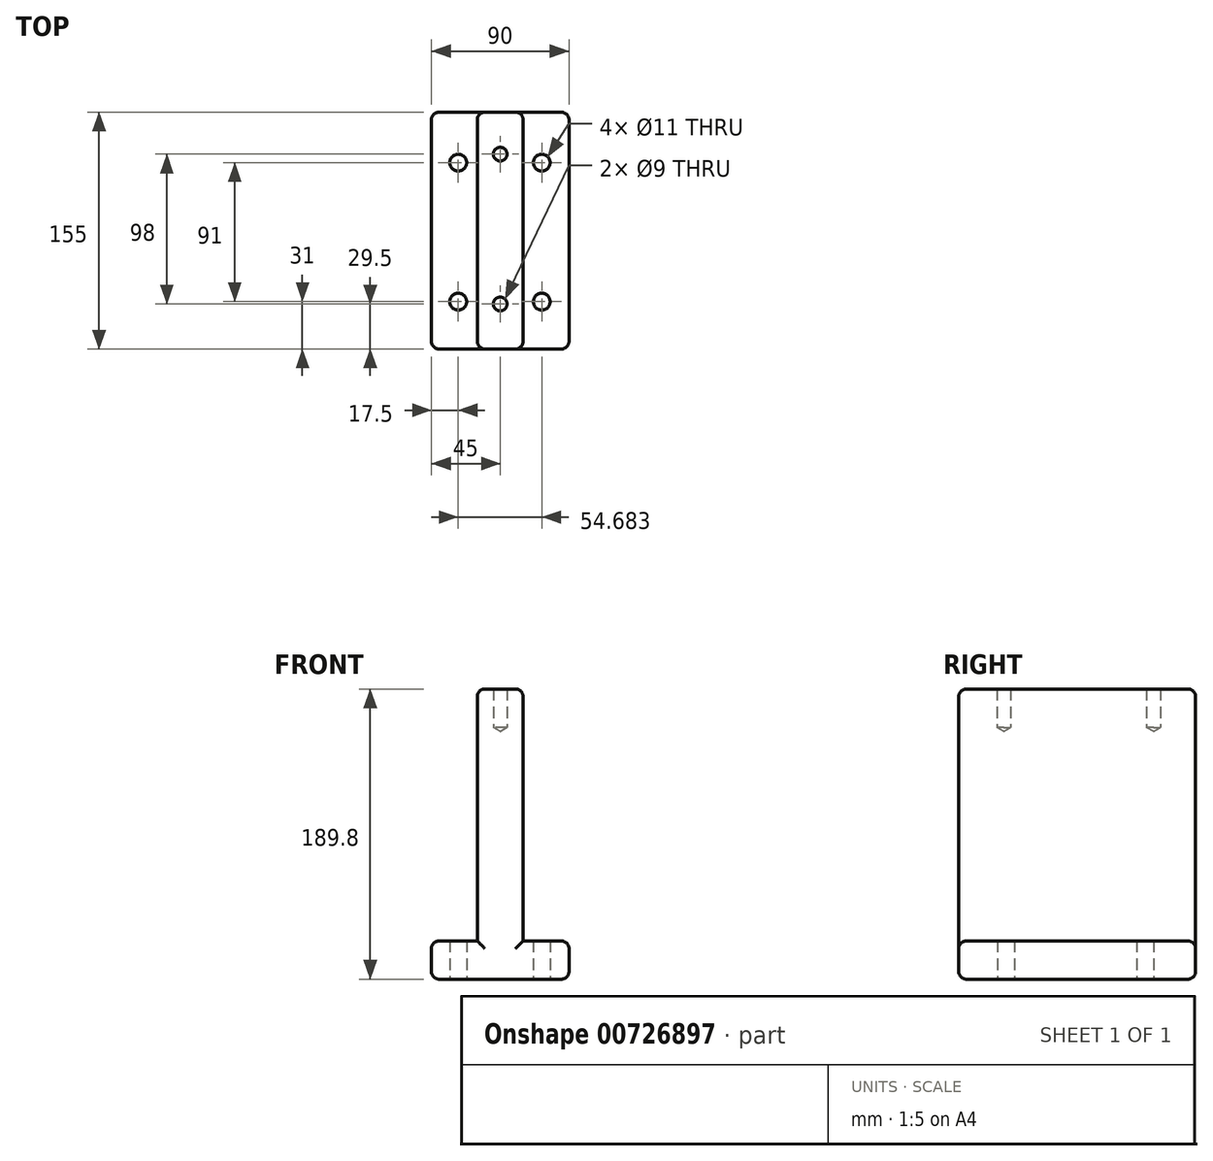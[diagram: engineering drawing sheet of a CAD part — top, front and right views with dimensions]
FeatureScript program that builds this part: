
annotation { "Feature Type Name" : "Feature", "Feature Type Description" : "" }
export const myFeature = defineFeature(function(context is Context, id is Id, definition is map)
    precondition{}
    {
        {
            var Q0;
            Q0=qCreatedBy(makeId("Front.planeOp"),FACE);
            var sketch = newSketch(context, id + "F0", { "sketchPlane" : qUnion([Q0])});
            skLineSegment(sketch, "E0", {"start": v(0, 0) * mm, "end": v(0, 189.8) * mm});
            skLineSegment(sketch, "E1", {"start": v(30, 0) * mm, "end": v(0, 0) * mm});
            skLineSegment(sketch, "E2", {"start": v(30, 0) * mm, "end": v(30, 189.8) * mm});
            skLineSegment(sketch, "E3", {"start": v(30, 189.8) * mm, "end": v(0, 189.8) * mm});
            skLineSegment(sketch, "E4", {"start": v(30, 0) * mm, "end": v(60, 0) * mm});
            skLineSegment(sketch, "E5", {"start": v(60, 0) * mm, "end": v(60, 25) * mm});
            skLineSegment(sketch, "E6", {"start": v(60, 25) * mm, "end": v(30, 25) * mm});
            skLineSegment(sketch, "E7", {"start": v(0, 0) * mm, "end": v(-30, 0) * mm});
            skLineSegment(sketch, "E8", {"start": v(-30, 0) * mm, "end": v(-30, 25) * mm});
            skLineSegment(sketch, "E9", {"start": v(-30, 25) * mm, "end": v(0, 25) * mm});
            skSolve(sketch);
        }
        {
            var Q0;
            Q0 = qSketchRegion(id + "F0", true);
            extrude(context, id + "F1", {"entities" : qUnion([Q0]), "depth" : 155 * mm, "offsetDistance" : 25 * mm});
        }
        {
            var Q0;
            Q0=makeQuery(id+"F1.opExtrude","CAP_EDGE",EDGE,{"disambiguationData":[OSD([sQuery(id+"F0.wireOp",EDGE,"E3")])],"isStart":false});
            var Q1;
            Q1=makeQuery(id+"F1.opExtrude","CAP_EDGE",EDGE,{"disambiguationData":[OSD([sQuery(id+"F0.wireOp",EDGE,"E0")])],"isStart":false});
            var Q2;
            Q2=makeQuery(id+"F1.opExtrude","CAP_EDGE",EDGE,{"disambiguationData":[OSD([sQuery(id+"F0.wireOp",EDGE,"E2")])],"isStart":false});
            var Q3;
            Q3=makeQuery(id+"F1.opExtrude","CAP_EDGE",EDGE,{"disambiguationData":[OSD([sQuery(id+"F0.wireOp",EDGE,"E6")])],"isStart":false});
            var Q4;
            Q4=makeQuery(id+"F1.opExtrude","CAP_EDGE",EDGE,{"disambiguationData":[OSD([sQuery(id+"F0.wireOp",EDGE,"E9")])],"isStart":false});
            var Q5;
            Q5=makeQuery(id+"F1.opExtrude","CAP_EDGE",EDGE,{"disambiguationData":[OSD([sQuery(id+"F0.wireOp",EDGE,"E8")])],"isStart":false});
            var Q6;
            Q6=makeQuery(id+"F1.opExtrude","CAP_EDGE",EDGE,{"disambiguationData":[OSD([sQuery(id+"F0.wireOp",EDGE,"E1"),sQuery(id+"F0.wireOp",EDGE,"E4"),sQuery(id+"F0.wireOp",EDGE,"E7")])],"isStart":false});
            var Q7;
            Q7=makeQuery(id+"F1.opExtrude","CAP_EDGE",EDGE,{"disambiguationData":[OSD([sQuery(id+"F0.wireOp",EDGE,"E5")])],"isStart":false});
            var Q8;
            Q8=makeQuery(id+"F1.opExtrude","SWEPT_EDGE",EDGE,{"disambiguationData":[OSD([sQuery(id+"F0.wireOp",EDGE,"E5"),sQuery(id+"F0.wireOp",EDGE,"E6")])]});
            var Q9;
            Q9=makeQuery(id+"F1.opExtrude","SWEPT_EDGE",EDGE,{"disambiguationData":[OSD([sQuery(id+"F0.wireOp",EDGE,"E4"),sQuery(id+"F0.wireOp",EDGE,"E5")])]});
            var Q10;
            Q10=makeQuery(id+"F1.opExtrude","SWEPT_EDGE",EDGE,{"disambiguationData":[OSD([sQuery(id+"F0.wireOp",EDGE,"E8"),sQuery(id+"F0.wireOp",EDGE,"E9")])]});
            var Q11;
            Q11=makeQuery(id+"F1.opExtrude","SWEPT_EDGE",EDGE,{"disambiguationData":[OSD([sQuery(id+"F0.wireOp",EDGE,"E7"),sQuery(id+"F0.wireOp",EDGE,"E8")])]});
            var Q12;
            Q12=makeQuery(id+"F1.opExtrude","SWEPT_EDGE",EDGE,{"disambiguationData":[OSD([sQuery(id+"F0.wireOp",EDGE,"E0"),sQuery(id+"F0.wireOp",EDGE,"E3")])]});
            var Q13;
            Q13=makeQuery(id+"F1.opExtrude","SWEPT_EDGE",EDGE,{"disambiguationData":[OSD([sQuery(id+"F0.wireOp",EDGE,"E2"),sQuery(id+"F0.wireOp",EDGE,"E3")])]});
            var Q14;
            Q14=makeQuery(id+"F1.opExtrude","CAP_EDGE",EDGE,{"disambiguationData":[OSD([sQuery(id+"F0.wireOp",EDGE,"E0")])],"isStart":true});
            var Q15;
            Q15=makeQuery(id+"F1.opExtrude","CAP_EDGE",EDGE,{"disambiguationData":[OSD([sQuery(id+"F0.wireOp",EDGE,"E2")])],"isStart":true});
            var Q16;
            Q16=makeQuery(id+"F1.opExtrude","CAP_EDGE",EDGE,{"disambiguationData":[OSD([sQuery(id+"F0.wireOp",EDGE,"E6")])],"isStart":true});
            var Q17;
            Q17=makeQuery(id+"F1.opExtrude","CAP_EDGE",EDGE,{"disambiguationData":[OSD([sQuery(id+"F0.wireOp",EDGE,"E1"),sQuery(id+"F0.wireOp",EDGE,"E4"),sQuery(id+"F0.wireOp",EDGE,"E7")])],"isStart":true});
            var Q18;
            Q18=makeQuery(id+"F1.opExtrude","CAP_EDGE",EDGE,{"disambiguationData":[OSD([sQuery(id+"F0.wireOp",EDGE,"E9")])],"isStart":true});
            var Q19;
            Q19=makeQuery(id+"F1.opExtrude","CAP_EDGE",EDGE,{"disambiguationData":[OSD([sQuery(id+"F0.wireOp",EDGE,"E8")])],"isStart":true});
            var Q20;
            Q20=makeQuery(id+"F1.opExtrude","CAP_EDGE",EDGE,{"disambiguationData":[OSD([sQuery(id+"F0.wireOp",EDGE,"E5")])],"isStart":true});
            var Q21;
            Q21=makeQuery(id+"F1.opExtrude","CAP_EDGE",EDGE,{"disambiguationData":[OSD([sQuery(id+"F0.wireOp",EDGE,"E3")])],"isStart":true});
            fillet(context, id + "F2", {"entities" : qUnion([Q0, Q1, Q2, Q3, Q4, Q5, Q6, Q7, Q8, Q9, Q10, Q11, Q12, Q13, Q14, Q15, Q16, Q17, Q18, Q19, Q20, Q21]), "radius" : 5 * mm, "tangentPropagation" : true, "allowEdgeOverflow" : false});
        }
        {
            var Q0;
            Q0=makeQuery(id+"F1.opExtrude","SWEPT_FACE",FACE,{"disambiguationData":[OSD([sQuery(id+"F0.wireOp",EDGE,"E3")])]});
            var sketch = newSketch(context, id + "F3", { "sketchPlane" : qUnion([Q0])});
            skLineSegment(sketch, "E10", {"start": v(0, 0) * mm, "end": v(15, 0) * mm});
            skLineSegment(sketch, "E11", {"start": v(15, 0) * mm, "end": v(15, -27.5) * mm});
            skLineSegment(sketch, "E12", {"start": v(15, -27.5) * mm, "end": v(15, -125.5) * mm});
            skPoint(sketch, "E13", {"position": v(15, -27.5) * mm});
            skPoint(sketch, "E14", {"position": v(15, -125.5) * mm});
            skSolve(sketch);
        }
        {
            var Q0;
            Q0=sQuery(id+"F3.wireOp",VERTEX,"E13");
            var Q1;
            Q1=sQuery(id+"F3.wireOp",VERTEX,"E14");
            var Q2;
            Q2=makeQuery(id+"F1.opExtrude","SWEPT_BODY",BODY,{"disambiguationData":[OSD([sQuery(id+"F0.wireOp",EDGE,"E0"),sQuery(id+"F0.wireOp",EDGE,"E1"),sQuery(id+"F0.wireOp",EDGE,"E2"),sQuery(id+"F0.wireOp",EDGE,"E3"),sQuery(id+"F0.wireOp",EDGE,"E4"),sQuery(id+"F0.wireOp",EDGE,"E5"),sQuery(id+"F0.wireOp",EDGE,"E6"),sQuery(id+"F0.wireOp",EDGE,"E7"),sQuery(id+"F0.wireOp",EDGE,"E8"),sQuery(id+"F0.wireOp",EDGE,"E9")])]});
            hole(context, id + "F4", {"style" : HoleStyle.SIMPLE, "endStyle" : HoleEndStyle.BLIND, "holeDiameter" : 9 * mm, "majorDiameter" : 5 * mm, "holeDepth" : 25 * mm, "isTappedThrough" : true, "tappedDepth" : 12 * mm, "tapClearance" : 3, "locations" : qUnion([Q0, Q1]), "scope" : qUnion([Q2])});
        }
        {
            var Q0;
            Q0=makeQuery(id+"F1.opExtrude","SWEPT_FACE",FACE,{"disambiguationData":[OSD([sQuery(id+"F0.wireOp",EDGE,"E9")])]});
            var sketch = newSketch(context, id + "F5", { "sketchPlane" : qUnion([Q0])});
            skLineSegment(sketch, "E15", {"start": v(0, 0) * mm, "end": v(-12.5, 0) * mm});
            skPoint(sketch, "E15.endSnap0", {"position": v(-12.5, -5) * mm});
            skLineSegment(sketch, "E16", {"start": v(-12.5, 0) * mm, "end": v(-12.5, -33) * mm});
            skLineSegment(sketch, "E17", {"start": v(-12.5, -33) * mm, "end": v(-12.5, -124) * mm});
            skPoint(sketch, "E18", {"position": v(-12.5, -33) * mm});
            skPoint(sketch, "E19", {"position": v(-12.5, -124) * mm});
            skLineSegment(sketch, "E20", {"start": v(0, 0) * mm, "end": v(42.18, 0) * mm});
            skLineSegment(sketch, "E21", {"start": v(42.18, 0) * mm, "end": v(42.18, -33) * mm});
            skLineSegment(sketch, "E22", {"start": v(42.18, -33) * mm, "end": v(42.18, -124) * mm});
            skPoint(sketch, "E23", {"position": v(42.18, -33) * mm});
            skPoint(sketch, "E24", {"position": v(42.18, -124) * mm});
            skSolve(sketch);
        }
        {
            var Q0;
            Q0=sQuery(id+"F5.wireOp",VERTEX,"E18");
            var Q1;
            Q1=sQuery(id+"F5.wireOp",VERTEX,"E19");
            var Q2;
            Q2=sQuery(id+"F5.wireOp",VERTEX,"E23");
            var Q3;
            Q3=sQuery(id+"F5.wireOp",VERTEX,"E24");
            var Q4;
            Q4=makeQuery(id+"F1.opExtrude","SWEPT_BODY",BODY,{"disambiguationData":[OSD([sQuery(id+"F0.wireOp",EDGE,"E0"),sQuery(id+"F0.wireOp",EDGE,"E1"),sQuery(id+"F0.wireOp",EDGE,"E2"),sQuery(id+"F0.wireOp",EDGE,"E3"),sQuery(id+"F0.wireOp",EDGE,"E4"),sQuery(id+"F0.wireOp",EDGE,"E5"),sQuery(id+"F0.wireOp",EDGE,"E6"),sQuery(id+"F0.wireOp",EDGE,"E7"),sQuery(id+"F0.wireOp",EDGE,"E8"),sQuery(id+"F0.wireOp",EDGE,"E9")])]});
            hole(context, id + "F6", {"style" : HoleStyle.SIMPLE, "endStyle" : HoleEndStyle.BLIND, "standardTappedOrClearance" : lookupTablePath({ "fit" : "Normal", "standard" : "ISO", "size" : "M10", "type" : "Clearance" }), "standardBlindInLast" : lookupTablePath({ "fit" : "Standard", "standard" : "ISO", "size" : "M10", "type" : "Clearance" }), "holeDiameter" : 11 * mm, "majorDiameter" : 5 * mm, "holeDepth" : 25 * mm, "isTappedThrough" : true, "tappedDepth" : 12 * mm, "tapClearance" : 3, "locations" : qUnion([Q0, Q1, Q2, Q3]), "scope" : qUnion([Q4])});
        }
    });
